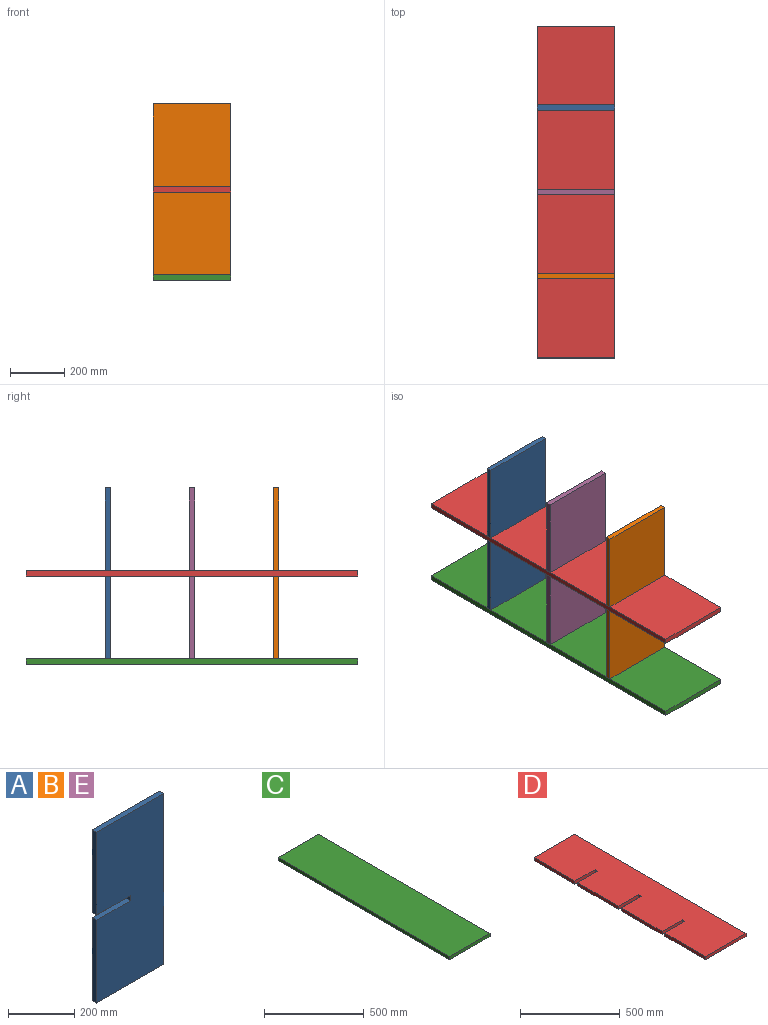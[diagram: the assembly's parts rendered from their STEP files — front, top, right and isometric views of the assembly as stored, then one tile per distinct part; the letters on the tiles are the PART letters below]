
ASSEMBLY  parts=5 mates=4
PART A: 10 faces, bbox 285.8x19.1x628.7 mm
  f0: plane 304.8x19.05mm, normal (-1,0,0), area 5806.4mm2, adj f1,f2,f5,f7
  f1: plane 628.65x285.75mm, normal (0,-1,0), area 176915mm2, adj f0,f3,f4,f5,f6,f7,f8,f9
  f2: plane 628.65x285.75mm, normal (0,1,0), area 176915mm2, adj f0,f3,f4,f5,f6,f7,f8,f9
  f3: plane 285.75x19.05mm, normal (0,0,-1), area 5443.5mm2, adj f1,f2,f4,f6
  f4: plane 628.65x19.05mm, normal (1,0,0), area 11975.8mm2, adj f1,f2,f3,f5
  f5: plane 285.75x19.05mm, normal (0,0,1), area 5443.5mm2, adj f0,f1,f2,f4
  f6: plane 304.8x19.05mm, normal (-1,0,0), area 5806.4mm2, adj f1,f2,f3,f8
  f7: plane 142.88x19.05mm, normal (0,0,-1), area 2721.8mm2, adj f0,f1,f2,f9
  f8: plane 142.88x19.05mm, normal (0,0,1), area 2721.8mm2, adj f1,f2,f6,f9
  f9: plane 19.05x19.05mm, normal (-1,0,0), area 362.9mm2, adj f1,f2,f7,f8
PART B: same geometry as A
PART C: 6 faces, bbox 285.8x1219.2x19.1 mm
  f0: plane 1219.2x19.05mm, normal (-1,0,0), area 23225.8mm2, adj f1,f3,f4,f5
  f1: plane 285.75x19.05mm, normal (0,-1,0), area 5443.5mm2, adj f0,f2,f4,f5
  f2: plane 1219.2x19.05mm, normal (1,0,0), area 23225.8mm2, adj f1,f3,f4,f5
  f3: plane 285.75x19.05mm, normal (0,1,0), area 5443.5mm2, adj f0,f2,f4,f5
  f4: plane 1219.2x285.75mm, normal (0,0,1), area 348386.4mm2, adj f0,f1,f2,f3
  f5: plane 1219.2x285.75mm, normal (0,0,-1), area 348386.4mm2, adj f0,f1,f2,f3
PART D: 18 faces, bbox 285.8x1219.2x19.1 mm
  f0: plane 290.51x19.05mm, normal (-1,0,0), area 5534.3mm2, adj f7,f8,f12,f17
  f1: plane 290.51x19.05mm, normal (-1,0,0), area 5534.3mm2, adj f7,f8,f9,f14
  f2: plane 290.51x19.05mm, normal (-1,0,0), area 5534.3mm2, adj f6,f7,f8,f11
  f3: plane 290.51x19.05mm, normal (-1,0,0), area 5534.3mm2, adj f4,f7,f8,f15
  f4: plane 285.75x19.05mm, normal (0,-1,0), area 5443.5mm2, adj f3,f5,f7,f8
  f5: plane 1219.2x19.05mm, normal (1,0,0), area 23225.8mm2, adj f4,f6,f7,f8
  f6: plane 285.75x19.05mm, normal (0,1,0), area 5443.5mm2, adj f2,f5,f7,f8
  f7: plane 1219.2x285.75mm, normal (0,0,1), area 340221.1mm2, adj f0,f1,f2,f3,f4,f5,f6,f9
  f8: plane 1219.2x285.75mm, normal (0,0,-1), area 340221.1mm2, adj f0,f1,f2,f3,f4,f5,f6,f9
  f9: plane 142.88x19.05mm, normal (0,1,0), area 2721.8mm2, adj f1,f7,f8,f10
  f10: plane 19.05x19.05mm, normal (-1,0,0), area 362.9mm2, adj f7,f8,f9,f11
  f11: plane 142.88x19.05mm, normal (0,-1,0), area 2721.8mm2, adj f2,f7,f8,f10
  f12: plane 142.88x19.05mm, normal (0,1,0), area 2721.8mm2, adj f0,f7,f8,f13
  f13: plane 19.05x19.05mm, normal (-1,0,0), area 362.9mm2, adj f7,f8,f12,f14
  f14: plane 142.88x19.05mm, normal (0,-1,0), area 2721.8mm2, adj f1,f7,f8,f13
  f15: plane 142.88x19.05mm, normal (0,1,0), area 2721.8mm2, adj f3,f7,f8,f16
  f16: plane 19.05x19.05mm, normal (-1,0,0), area 362.9mm2, adj f7,f8,f15,f17
  f17: plane 142.88x19.05mm, normal (0,-1,0), area 2721.8mm2, adj f0,f7,f8,f16
PART E: same geometry as A
PLACE A t=(-370.98,430.52,-1381.87)mm
PLACE B t=(-370.98,-188.61,-1381.87)mm
PLACE C t=(-370.98,120.96,-1705.72)mm
PLACE D rot(axis=(0,1,0),180deg) t=(-370.98,120.96,-1381.87)mm
PLACE E t=(-370.98,120.96,-1381.87)mm
MATE fastened A.f9 <-> D.f10  axis (-1,0,0) through (-370.98,430.52,-1381.87)mm
MATE fastened E.f9 <-> D.f13  axis (-1,0,0) through (-370.98,120.96,-1381.87)mm
MATE fastened C.f4 <-> E.f3  axis (0,0,1) through (-370.98,120.96,-1696.19)mm
MATE fastened D.f16 <-> B.f9  axis (1,0,0) through (-370.98,-188.61,-1381.87)mm
